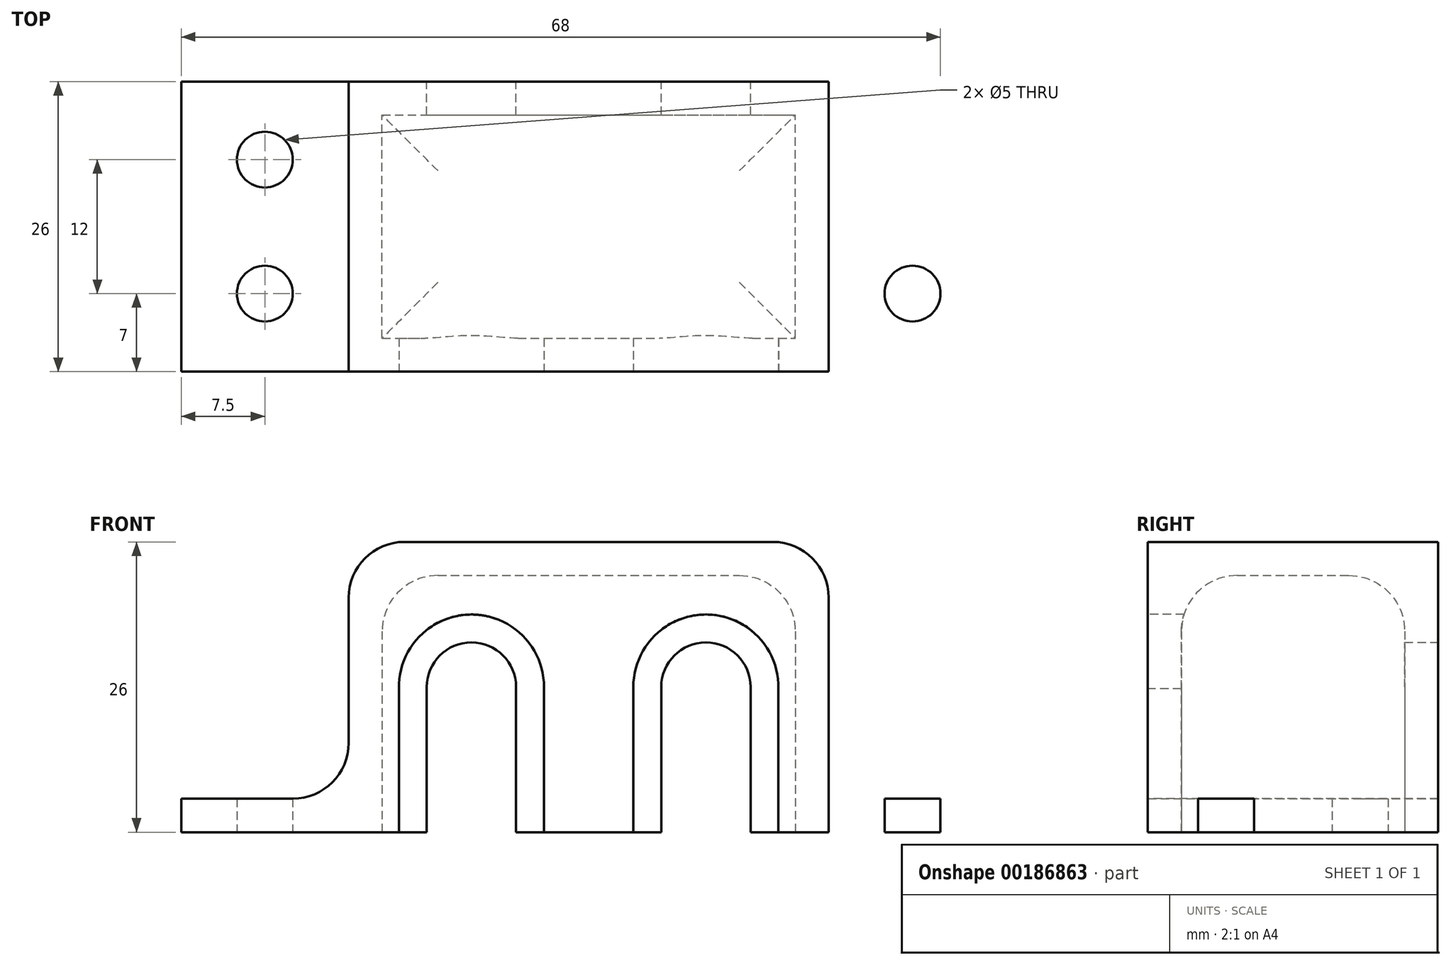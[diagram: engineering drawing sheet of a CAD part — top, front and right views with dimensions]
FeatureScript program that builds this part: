
annotation { "Feature Type Name" : "Feature", "Feature Type Description" : "" }
export const myFeature = defineFeature(function(context is Context, id is Id, definition is map)
    precondition{}
    {
        {
            var Q0;
            Q0=qCreatedBy(makeId("Front.planeOp"),FACE);
            var sketch = newSketch(context, id + "F0", { "sketchPlane" : qUnion([Q0])});
            skLineSegment(sketch, "E0.bottom", {"start": v(-21.5, 10.65) * mm, "end": v(21.5, 10.65) * mm});
            skLineSegment(sketch, "E0.top", {"start": v(-21.5, -10.65) * mm, "end": v(21.5, -10.65) * mm});
            skLineSegment(sketch, "E0.left", {"start": v(-21.5, 10.65) * mm, "end": v(-21.5, -10.65) * mm});
            skLineSegment(sketch, "E0.right", {"start": v(21.5, 10.65) * mm, "end": v(21.5, -10.65) * mm});
            skPoint(sketch, "E0.middle", {"position": v(0, 0) * mm});
            skCircle(sketch, "E1", {"center": v(-10.5, 0) * mm, "radius": 6.5 * mm});
            skCircle(sketch, "E2.MirrorC", {"center": v(10.5, 0) * mm, "radius": 6.5 * mm});
            skSolve(sketch);
        }
        {
            var Q0;
            Q0=qCreatedBy(makeId("Top.planeOp"),FACE);
            var sketch = newSketch(context, id + "F1", { "sketchPlane" : qUnion([Q0])});
            skPoint(sketch, "E3.0", {"position": v(-21.5, 0) * mm});
            skPoint(sketch, "E4.0", {"position": v(21.5, 0) * mm});
            skLineSegment(sketch, "E5.bottom", {"start": v(-21.5, 0) * mm, "end": v(21.5, 0) * mm});
            skLineSegment(sketch, "E5.top", {"start": v(-21.5, 26) * mm, "end": v(21.5, 26) * mm});
            skLineSegment(sketch, "E5.left", {"start": v(-21.5, 0) * mm, "end": v(-21.5, 26) * mm});
            skLineSegment(sketch, "E5.right", {"start": v(21.5, 0) * mm, "end": v(21.5, 26) * mm});
            skSolve(sketch);
        }
        {
            var Q0;
            Q0=qSketchRegion(id+"F1",true);
            extrude(context, id + "F2", {"entities" : qUnion([Q0]), "depth" : 13 * mm, "offsetDistance" : 25 * mm, "hasSecondDirection" : true, "secondDirectionOppositeDirection" : true, "secondDirectionDepth" : 13 * mm});
        }
        {
            var Q0;
            Q0=makeQuery(id+"F2.opExtrude","CAP_FACE",FACE,{"disambiguationData":[OSD([sQuery(id+"F1.wireOp",EDGE,"E5.bottom"),sQuery(id+"F1.wireOp",EDGE,"E5.top"),sQuery(id+"F1.wireOp",EDGE,"E5.left"),sQuery(id+"F1.wireOp",EDGE,"E5.right")])],"isStart":true});
            shell(context, id + "F3", {"entities" : qUnion([Q0]), "thickness" : 3 * mm});
        }
        {
            var Q0;
            Q0=makeQuery(id+"F2.opExtrude","SWEPT_FACE",FACE,{"disambiguationData":[OSD([sQuery(id+"F1.wireOp",EDGE,"E5.top")])]});
            var sketch = newSketch(context, id + "F4", { "sketchPlane" : qUnion([Q0])});
            skPoint(sketch, "E6.0", {"position": v(-10.5, 0) * mm});
            skPoint(sketch, "E7.0", {"position": v(10.5, 0) * mm});
            skArc(sketch, "E8", {"start": v(-6.5, 0) * mm, "mid": v(-10.5, 4) * mm, "end": v(-14.5, 0) * mm});
            skArc(sketch, "E9.MirrorC", {"start": v(6.5, 0) * mm, "mid": v(10.5, 4) * mm, "end": v(14.5, 0) * mm});
            skLineSegment(sketch, "E10", {"start": v(-14.5, 0) * mm, "end": v(-14.5, -13) * mm});
            skLineSegment(sketch, "E11", {"start": v(-6.5, 0) * mm, "end": v(-6.5, -13) * mm});
            skLineSegment(sketch, "E12.MirrorCS", {"start": v(6.5, 0) * mm, "end": v(6.5, -13) * mm});
            skLineSegment(sketch, "E13.MirrorCS", {"start": v(14.5, 0) * mm, "end": v(14.5, -13) * mm});
            skLineSegment(sketch, "E14", {"start": v(-14.5, -13) * mm, "end": v(-6.5, -13) * mm});
            skLineSegment(sketch, "E15", {"start": v(6.5, -13) * mm, "end": v(14.5, -13) * mm});
            skSolve(sketch);
        }
        {
            var Q0;
            Q0=makeQuery(id+"F2.opExtrude","CAP_FACE",FACE,{"disambiguationData":[OSD([sQuery(id+"F1.wireOp",EDGE,"E5.bottom"),sQuery(id+"F1.wireOp",EDGE,"E5.top"),sQuery(id+"F1.wireOp",EDGE,"E5.left"),sQuery(id+"F1.wireOp",EDGE,"E5.right")])],"isStart":true});
            var sketch = newSketch(context, id + "F5", { "sketchPlane" : qUnion([Q0])});
            skLineSegment(sketch, "E16.bottom", {"start": v(-21.5, 0) * mm, "end": v(-36.5, 0) * mm});
            skLineSegment(sketch, "E16.top", {"start": v(-21.5, -26) * mm, "end": v(-36.5, -26) * mm});
            skLineSegment(sketch, "E16.left", {"start": v(-21.5, 0) * mm, "end": v(-21.5, -26) * mm});
            skLineSegment(sketch, "E16.right", {"start": v(-36.5, 0) * mm, "end": v(-36.5, -26) * mm});
            skLineSegment(sketch, "E17", {"start": v(-29, 0) * mm, "end": v(-29, -26) * mm, "construction": true});
            skCircle(sketch, "E18", {"center": v(-29, -7) * mm, "radius": 2.5 * mm});
            skLineSegment(sketch, "E19", {"start": v(-36.5, -13) * mm, "end": v(-21.5, -13) * mm, "construction": true});
            skCircle(sketch, "E20.MirrorC", {"center": v(-29, -19) * mm, "radius": 2.5 * mm});
            skCircle(sketch, "E21.MirrorC", {"center": v(29, -7) * mm, "radius": 2.5 * mm});
            skCircle(sketch, "E22.MirrorC", {"center": v(29, -19) * mm, "radius": 2.5 * mm});
            skLineSegment(sketch, "E23.MirrorCS", {"start": v(21.5, 0) * mm, "end": v(36.5, 0) * mm});
            skLineSegment(sketch, "E24.MirrorCS", {"start": v(36.5, 0) * mm, "end": v(36.5, -26) * mm});
            skLineSegment(sketch, "E25.MirrorCS", {"start": v(21.5, -26) * mm, "end": v(36.5, -26) * mm});
            skLineSegment(sketch, "E26.0.0", {"start": v(-21.5, -26) * mm, "end": v(21.5, -26) * mm});
            skLineSegment(sketch, "E26.0.1", {"start": v(21.5, -26) * mm, "end": v(21.5, 0) * mm});
            skLineSegment(sketch, "E26.0.2", {"start": v(21.5, 0) * mm, "end": v(-21.5, 0) * mm});
            skSolve(sketch);
        }
        {
            var Q0;
            Q0=makeQuery(id+"F5.imprint","IMPRINT",FACE,{"disambiguationData":[TD([[makeQuery(id+"F5.imprint","IMPRINT",EDGE,{"derivedFrom":sQuery(id+"F5.wireOp",EDGE,"E16.bottom")}),1.0]])]});
            var Q1;
            Q1=makeQuery(id+"F5.imprint","IMPRINT",FACE,{"disambiguationData":[TD([[makeQuery(id+"F5.imprint","IMPRINT",EDGE,{"derivedFrom":sQuery(id+"F5.wireOp",EDGE,"E26.0.0")}),1.0]])]});
            var Q2;
            Q2=makeQuery(id+"F5.imprint","IMPRINT",FACE,{"disambiguationData":[TD([[makeQuery(id+"F5.imprint","IMPRINT",EDGE,{"derivedFrom":sQuery(id+"F5.wireOp",EDGE,"E21.MirrorC")}),1.0]])]});
            extrude(context, id + "F6", {"entities" : qUnion([Q0, Q1, Q2]), "operationType" : NewBodyOperationType.ADD, "oppositeDirection" : true, "depth" : 3 * mm, "offsetDistance" : 25 * mm});
        }
        {
            var Q0;
            Q0=makeQuery(id+"F2.opExtrude","CAP_EDGE",EDGE,{"disambiguationData":[OSD([sQuery(id+"F1.wireOp",EDGE,"E5.left")])],"isStart":false});
            var Q1;
            Q1=makeQuery(id+"F2.opExtrude","CAP_EDGE",EDGE,{"disambiguationData":[OSD([sQuery(id+"F1.wireOp",EDGE,"E5.right")])],"isStart":false});
            var Q2;
            {var subQ0=sQuery(id+"F1.wireOp",EDGE,"E5.left");Q2=makeQuery(id+"F6.boolean.opBoolean","INTERSECT",EDGE,{"derivedFrom":[makeQuery(id+"F2.opExtrude","SWEPT_FACE",FACE,{"disambiguationData":[OSD([subQ0])]}),makeQuery(id+"F6.opExtrude","CAP_FACE",FACE,{"disambiguationData":[OSD([sQuery(id+"F1.wireOp",EDGE,"E5.bottom"),sQuery(id+"F1.wireOp",EDGE,"E5.top"),subQ0,sQuery(id+"F1.wireOp",EDGE,"E5.right"),sQuery(id+"F5.wireOp",EDGE,"E16.bottom"),sQuery(id+"F5.wireOp",EDGE,"E16.top"),sQuery(id+"F5.wireOp",EDGE,"E16.right"),sQuery(id+"F5.wireOp",EDGE,"E18"),sQuery(id+"F5.wireOp",EDGE,"E20.MirrorC"),sQuery(id+"F5.wireOp",EDGE,"E21.MirrorC"),sQuery(id+"F5.wireOp",EDGE,"E22.MirrorC"),sQuery(id+"F5.wireOp",EDGE,"E23.MirrorCS"),sQuery(id+"F5.wireOp",EDGE,"E24.MirrorCS"),sQuery(id+"F5.wireOp",EDGE,"E25.MirrorCS"),sQuery(id+"F5.wireOp",EDGE,"E26.0.0"),sQuery(id+"F5.wireOp",EDGE,"E26.0.2")])],"isStart":false})]});}
            var Q3;
            {var subQ0=sQuery(id+"F1.wireOp",EDGE,"E5.right");Q3=makeQuery(id+"F6.boolean.opBoolean","INTERSECT",EDGE,{"derivedFrom":[makeQuery(id+"F2.opExtrude","SWEPT_FACE",FACE,{"disambiguationData":[OSD([subQ0])]}),makeQuery(id+"F6.opExtrude","CAP_FACE",FACE,{"disambiguationData":[OSD([sQuery(id+"F1.wireOp",EDGE,"E5.bottom"),sQuery(id+"F1.wireOp",EDGE,"E5.top"),sQuery(id+"F1.wireOp",EDGE,"E5.left"),subQ0,sQuery(id+"F5.wireOp",EDGE,"E16.bottom"),sQuery(id+"F5.wireOp",EDGE,"E16.top"),sQuery(id+"F5.wireOp",EDGE,"E16.right"),sQuery(id+"F5.wireOp",EDGE,"E18"),sQuery(id+"F5.wireOp",EDGE,"E20.MirrorC"),sQuery(id+"F5.wireOp",EDGE,"E21.MirrorC"),sQuery(id+"F5.wireOp",EDGE,"E22.MirrorC"),sQuery(id+"F5.wireOp",EDGE,"E23.MirrorCS"),sQuery(id+"F5.wireOp",EDGE,"E24.MirrorCS"),sQuery(id+"F5.wireOp",EDGE,"E25.MirrorCS"),sQuery(id+"F5.wireOp",EDGE,"E26.0.0"),sQuery(id+"F5.wireOp",EDGE,"E26.0.2")])],"isStart":false})]});}
            var Q4;
            {var subQ0=sQuery(id+"F1.wireOp",EDGE,"E5.top");Q4=makeQuery(id+"F3.opShell","OFFSET_EDGE",EDGE,{"disambiguationData":[OSD([subQ0]),TDD([makeQuery(id+"F2.opExtrude","CAP_EDGE",EDGE,{"disambiguationData":[OSD([subQ0])],"isStart":false})])]});}
            var Q5;
            {var subQ0=sQuery(id+"F1.wireOp",EDGE,"E5.bottom");Q5=makeQuery(id+"F3.opShell","OFFSET_EDGE",EDGE,{"disambiguationData":[OSD([subQ0]),TDD([makeQuery(id+"F2.opExtrude","CAP_EDGE",EDGE,{"disambiguationData":[OSD([subQ0])],"isStart":false})])]});}
            var Q6;
            {var subQ0=sQuery(id+"F1.wireOp",EDGE,"E5.left");Q6=makeQuery(id+"F3.opShell","OFFSET_EDGE",EDGE,{"disambiguationData":[OSD([subQ0]),TDD([makeQuery(id+"F2.opExtrude","CAP_EDGE",EDGE,{"disambiguationData":[OSD([subQ0])],"isStart":false})])]});}
            var Q7;
            {var subQ0=sQuery(id+"F1.wireOp",EDGE,"E5.right");Q7=makeQuery(id+"F3.opShell","OFFSET_EDGE",EDGE,{"disambiguationData":[OSD([subQ0]),TDD([makeQuery(id+"F2.opExtrude","CAP_EDGE",EDGE,{"disambiguationData":[OSD([subQ0])],"isStart":false})])]});}
            fillet(context, id + "F7", {"entities" : qUnion([Q0, Q1, Q2, Q3, Q4, Q5, Q6, Q7]), "radius" : 5 * mm, "tangentPropagation" : true, "allowEdgeOverflow" : false});
        }
        {
            var Q0;
            Q0=makeQuery(id+"F0.imprint","IMPRINT",FACE,{"disambiguationData":[TD([[makeQuery(id+"F0.imprint","IMPRINT",EDGE,{"derivedFrom":sQuery(id+"F0.wireOp",EDGE,"E0.bottom")}),-1.0]])]});
            var sketch = newSketch(context, id + "F8", { "sketchPlane" : qUnion([Q0])});
            skArc(sketch, "E27.0", {"start": v(-4, -0.03) * mm, "mid": v(-10.56, 6.5) * mm, "end": v(-17, -0.15) * mm});
            skArc(sketch, "E28.0", {"start": v(4, -0.03) * mm, "mid": v(10.56, 6.5) * mm, "end": v(17, -0.15) * mm});
            skLineSegment(sketch, "E29", {"start": v(-17, -0.15) * mm, "end": v(-17, -10.98) * mm});
            skLineSegment(sketch, "E30", {"start": v(-4, 0.03) * mm, "end": v(-4, -11) * mm});
            skLineSegment(sketch, "E31.MirrorCS", {"start": v(4, 0.03) * mm, "end": v(4, -11) * mm});
            skLineSegment(sketch, "E32.MirrorCS", {"start": v(17, -0.15) * mm, "end": v(17, -10.98) * mm});
            skLineSegment(sketch, "E33", {"start": v(-17, -10.98) * mm, "end": v(-17, -13) * mm});
            skLineSegment(sketch, "E34", {"start": v(-17, -13) * mm, "end": v(-4, -13) * mm});
            skLineSegment(sketch, "E35", {"start": v(-4, -13) * mm, "end": v(-4, -11) * mm});
            skLineSegment(sketch, "E36.MirrorCS", {"start": v(4, -13) * mm, "end": v(4, -11) * mm});
            skLineSegment(sketch, "E37.MirrorCS", {"start": v(17, -10.98) * mm, "end": v(17, -13) * mm});
            skLineSegment(sketch, "E38.MirrorCS", {"start": v(17, -13) * mm, "end": v(4, -13) * mm});
            skSolve(sketch);
        }
        {
            var Q0;
            Q0=qSketchRegion(id+"F8",true);
            extrude(context, id + "F9", {"entities" : qUnion([Q0]), "operationType" : NewBodyOperationType.REMOVE, "oppositeDirection" : true, "depth" : 5 * mm, "offsetDistance" : 25 * mm});
        }
        {
            var Q0;
            Q0=qSketchRegion(id+"F4",true);
            extrude(context, id + "F10", {"entities" : qUnion([Q0]), "operationType" : NewBodyOperationType.REMOVE, "oppositeDirection" : true, "depth" : 25 * mm, "offsetDistance" : 25 * mm});
        }
    });
